# Revit family: Faucet-Two_Handle-American_Standard-Fluent-7186.201_Series
name_source: partatom
category: Plumbing Fixtures
revit_build: Autodesk Revit 2018 (Build: 20170223_1515(x64)
units: mm (PartAtom-declared; Revit-internal decimal feet)

## family parameters
Always vertical = No
Cut with Voids When Loaded = No
OmniClass Number = 23.45.55.17
OmniClass Title = Mixing Faucets
Part Type = Normal
Room Calculation Point = No
Round Connector Dimension = Use Diameter
Shared = Yes
Work Plane-Based = Yes

## types (3) — shared parameters
ADA Compliant = Yes
Assembly Code = D2020300
CEC Compliant = Yes
CW Connection = Yes
CWFU = 1.5
CalGreen Compliant = Yes
Cold Water Connection Diameter = 1/2"
Default Elevation = 0"
Description = Fluent® 4-Inch Centerset 2-Handle Bathroom Faucet 1.2 gpm/4.5 L/min With Lever Handles
Flow Rate = 1.2 GPM (4.5 LPM)
HW Connection = Yes
HWFU = 1.5
Height = 6 5/8"
Hot Water Connection Diameter = 1/2"
IAPMO Compliance = Product meet or exceeds A112.18.1,NSF 61/Section 9 and Annex G,CSA B125.1
Installation Type = Deck Mounted
Length = 6 1/8"
Manufacturer = American Standard
Metal Speed Connect® Pop-Up Drain = Yes
Price = Prices may vary. Please consult Manufacturer Representative for most up-to-date price list.
Product Documentation Link = https://americanstandard.box.com
Product Page URL = https://www.americanstandard-us.com
Revised Date = 09/23/2021
Spout Reach = 4 5/16"
Type Comments = Metal Speed Connect® pop-up drain. Metal lever handles.
URL = http://www.americanstandard-us.com
Vent Connection = No
WFU = 2
Waste Connection = No
Width = 9 1/2"

## per-type parameters (varying)
| type | Handles Material | Material | Spout Material |
| 7186.201.002 | Metal-American Standard-002-Polished Chrome | Cast Brass-American Standard-002-Polished Chrome | Cast Brass-American Standard-002-Polished Chrome |
| 7186.201.278 | Metal-American Standard-278-Legacy Bronze | Cast Brass-American Standard-278-Legacy Bronze | Cast Brass-American Standard-278-Legacy Bronze |
| 7186.201.295 | Metal-American Standard-295-Brushed Nickel | Cast Brass-American Standard-295-Brushed Nickel | Cast Brass-American Standard-295-Brushed Nickel |

note: column(s) folded — value = type name in every type: Model

## geometry (parser evidence)
native form markers: Sweep x2
no freeform markers — native parametric forms only
